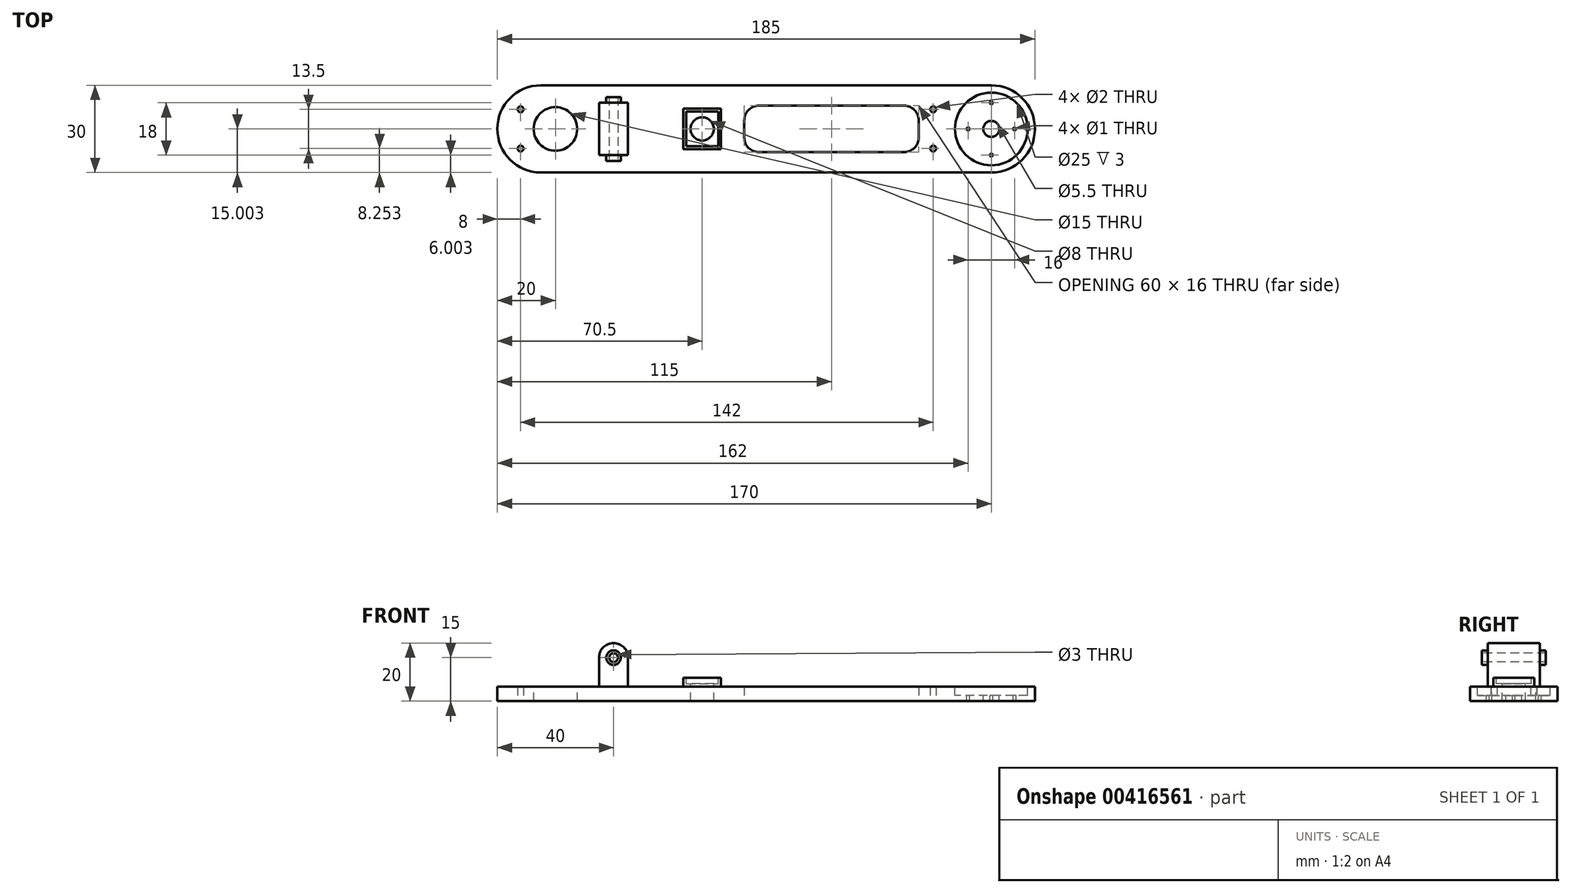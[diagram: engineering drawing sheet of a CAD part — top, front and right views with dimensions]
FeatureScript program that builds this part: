
annotation { "Feature Type Name" : "Feature", "Feature Type Description" : "" }
export const myFeature = defineFeature(function(context is Context, id is Id, definition is map)
    precondition{}
    {
        {
            var Q0;
            Q0=qCreatedBy(makeId("Top.planeOp"),FACE);
            var sketch = newSketch(context, id + "F0", { "sketchPlane" : qUnion([Q0])});
            skLineSegment(sketch, "E0.bottom", {"start": v(-85, 3.1) * mm, "end": v(100, 3.1) * mm});
            skLineSegment(sketch, "E0.top", {"start": v(-85, -26.9) * mm, "end": v(100, -26.9) * mm});
            skLineSegment(sketch, "E0.left", {"start": v(-85, 3.1) * mm, "end": v(-85, -26.9) * mm});
            skLineSegment(sketch, "E0.right", {"start": v(100, 3.1) * mm, "end": v(100, -26.9) * mm});
            skCircle(sketch, "E1", {"center": v(65, -5.15) * mm, "radius": 1 * mm});
            skCircle(sketch, "E2", {"center": v(65, -18.65) * mm, "radius": 1 * mm});
            skCircle(sketch, "E3", {"center": v(-77, -5.15) * mm, "radius": 1 * mm});
            skCircle(sketch, "E4", {"center": v(-77, -18.65) * mm, "radius": 1 * mm});
            skLineSegment(sketch, "E5.bottom", {"start": v(0, -3.9) * mm, "end": v(60, -3.9) * mm});
            skLineSegment(sketch, "E5.top", {"start": v(0, -19.9) * mm, "end": v(60, -19.9) * mm});
            skLineSegment(sketch, "E5.left", {"start": v(0, -3.9) * mm, "end": v(0, -19.9) * mm});
            skLineSegment(sketch, "E5.right", {"start": v(60, -3.9) * mm, "end": v(60, -19.9) * mm});
            skSolve(sketch);
        }
        {
            var Q0;
            Q0=makeQuery(id+"F0.imprint","IMPRINT",FACE,{"disambiguationData":[TD([[makeQuery(id+"F0.imprint","IMPRINT",EDGE,{"derivedFrom":sQuery(id+"F0.wireOp",EDGE,"E0.bottom")}),-1.0]])]});
            extrude(context, id + "F1", {"entities" : qUnion([Q0]), "depth" : 5 * mm});
        }
        {
            var Q0;
            Q0=makeQuery(id+"F1.opExtrude","CAP_FACE",FACE,{"disambiguationData":[OSD([sQuery(id+"F0.wireOp",EDGE,"E0.bottom"),sQuery(id+"F0.wireOp",EDGE,"E0.top"),sQuery(id+"F0.wireOp",EDGE,"E0.left"),sQuery(id+"F0.wireOp",EDGE,"E0.right")])],"isStart":false});
            var sketch = newSketch(context, id + "F2", { "sketchPlane" : qUnion([Q0])});
            skCircle(sketch, "E6", {"center": v(85, -11.9) * mm, "radius": 12.5 * mm});
            skCircle(sketch, "E7", {"center": v(85, -11.9) * mm, "radius": 2.75 * mm});
            skCircle(sketch, "E8", {"center": v(85, -2.9) * mm, "radius": 0.5 * mm});
            skCircle(sketch, "E9", {"center": v(85, -20.9) * mm, "radius": 0.5 * mm});
            skCircle(sketch, "E10", {"center": v(93, -11.9) * mm, "radius": 0.5 * mm});
            skCircle(sketch, "E11", {"center": v(77, -11.9) * mm, "radius": 0.5 * mm});
            skCircle(sketch, "E12", {"center": v(-65, -11.9) * mm, "radius": 7.5 * mm});
            skLineSegment(sketch, "E13.bottom", {"start": v(-50, -2.9) * mm, "end": v(-40, -2.9) * mm});
            skLineSegment(sketch, "E13.top", {"start": v(-50, -20.9) * mm, "end": v(-40, -20.9) * mm});
            skLineSegment(sketch, "E13.left", {"start": v(-50, -2.9) * mm, "end": v(-50, -20.9) * mm});
            skLineSegment(sketch, "E13.right", {"start": v(-40, -2.9) * mm, "end": v(-40, -20.9) * mm});
            skLineSegment(sketch, "E14.bottom", {"start": v(-21, -4.9) * mm, "end": v(-8, -4.9) * mm});
            skLineSegment(sketch, "E14.top", {"start": v(-21, -18.9) * mm, "end": v(-8, -18.9) * mm});
            skLineSegment(sketch, "E14.left", {"start": v(-21, -4.9) * mm, "end": v(-21, -18.9) * mm});
            skLineSegment(sketch, "E14.right", {"start": v(-8, -4.9) * mm, "end": v(-8, -18.9) * mm});
            skSolve(sketch);
        }
        {
            var Q0;
            Q0=makeQuery(id+"F2.imprint","IMPRINT",FACE,{"disambiguationData":[TD([[makeQuery(id+"F2.imprint","IMPRINT",EDGE,{"derivedFrom":sQuery(id+"F2.wireOp",EDGE,"E6")}),1.0]])]});
            extrude(context, id + "F3", {"entities" : qUnion([Q0]), "operationType" : NewBodyOperationType.REMOVE, "oppositeDirection" : true, "depth" : 3 * mm});
        }
        {
            var Q0;
            Q0=makeQuery(id+"F2.imprint","IMPRINT",FACE,{"disambiguationData":[TD([[makeQuery(id+"F2.imprint","IMPRINT",EDGE,{"derivedFrom":sQuery(id+"F2.wireOp",EDGE,"E7")}),1.0]])]});
            var Q1;
            Q1=makeQuery(id+"F2.imprint","IMPRINT",FACE,{"disambiguationData":[TD([[makeQuery(id+"F2.imprint","IMPRINT",EDGE,{"derivedFrom":sQuery(id+"F2.wireOp",EDGE,"E8")}),1.0]])]});
            var Q2;
            Q2=makeQuery(id+"F2.imprint","IMPRINT",FACE,{"disambiguationData":[TD([[makeQuery(id+"F2.imprint","IMPRINT",EDGE,{"derivedFrom":sQuery(id+"F2.wireOp",EDGE,"E11")}),1.0]])]});
            var Q3;
            Q3=makeQuery(id+"F2.imprint","IMPRINT",FACE,{"disambiguationData":[TD([[makeQuery(id+"F2.imprint","IMPRINT",EDGE,{"derivedFrom":sQuery(id+"F2.wireOp",EDGE,"E9")}),1.0]])]});
            var Q4;
            Q4=makeQuery(id+"F2.imprint","IMPRINT",FACE,{"disambiguationData":[TD([[makeQuery(id+"F2.imprint","IMPRINT",EDGE,{"derivedFrom":sQuery(id+"F2.wireOp",EDGE,"E10")}),1.0]])]});
            extrude(context, id + "F4", {"entities" : qUnion([Q0, Q1, Q2, Q3, Q4]), "operationType" : NewBodyOperationType.REMOVE, "oppositeDirection" : true, "depth" : 25 * mm});
        }
        {
            var Q0;
            Q0=makeQuery(id+"F1.opExtrude","SWEPT_EDGE",EDGE,{"disambiguationData":[OSD([sQuery(id+"F0.wireOp",EDGE,"E0.bottom"),sQuery(id+"F0.wireOp",EDGE,"E0.right")])]});
            var Q1;
            Q1=makeQuery(id+"F1.opExtrude","SWEPT_EDGE",EDGE,{"disambiguationData":[OSD([sQuery(id+"F0.wireOp",EDGE,"E0.top"),sQuery(id+"F0.wireOp",EDGE,"E0.right")])]});
            var Q2;
            Q2=makeQuery(id+"F1.opExtrude","SWEPT_EDGE",EDGE,{"disambiguationData":[OSD([sQuery(id+"F0.wireOp",EDGE,"E0.top"),sQuery(id+"F0.wireOp",EDGE,"E0.left")])]});
            var Q3;
            Q3=makeQuery(id+"F1.opExtrude","SWEPT_EDGE",EDGE,{"disambiguationData":[OSD([sQuery(id+"F0.wireOp",EDGE,"E0.bottom"),sQuery(id+"F0.wireOp",EDGE,"E0.left")])]});
            fillet(context, id + "F5", {"entities" : qUnion([Q0, Q1, Q2, Q3]), "radius" : 15 * mm, "tangentPropagation" : true, "allowEdgeOverflow" : false});
        }
        {
            var Q0;
            Q0=makeQuery(id+"F2.imprint","IMPRINT",FACE,{"disambiguationData":[TD([[makeQuery(id+"F2.imprint","IMPRINT",EDGE,{"derivedFrom":sQuery(id+"F2.wireOp",EDGE,"E12")}),1.0]])]});
            extrude(context, id + "F6", {"entities" : qUnion([Q0]), "operationType" : NewBodyOperationType.REMOVE, "oppositeDirection" : true, "depth" : 25 * mm});
        }
        {
            var Q0;
            Q0=makeQuery(id+"F2.imprint","IMPRINT",FACE,{"disambiguationData":[TD([[makeQuery(id+"F2.imprint","IMPRINT",EDGE,{"derivedFrom":sQuery(id+"F2.wireOp",EDGE,"E13.bottom")}),-1.0]])]});
            extrude(context, id + "F7", {"entities" : qUnion([Q0]), "operationType" : NewBodyOperationType.ADD, "depth" : 15 * mm});
        }
        {
            var Q0;
            Q0=makeQuery(id+"F7.opExtrude","CAP_EDGE",EDGE,{"disambiguationData":[OSD([sQuery(id+"F2.wireOp",EDGE,"E13.left")])],"isStart":true});
            var Q1;
            Q1=makeQuery(id+"F7.opExtrude","CAP_EDGE",EDGE,{"disambiguationData":[OSD([sQuery(id+"F2.wireOp",EDGE,"E13.right")])],"isStart":false});
            var Q2;
            Q2=makeQuery(id+"F7.opExtrude","CAP_EDGE",EDGE,{"disambiguationData":[OSD([sQuery(id+"F2.wireOp",EDGE,"E13.left")])],"isStart":false});
            var Q3;
            Q3=makeQuery(id+"F7.opExtrude","CAP_EDGE",EDGE,{"disambiguationData":[OSD([sQuery(id+"F2.wireOp",EDGE,"E13.right")])],"isStart":true});
            fillet(context, id + "F8", {"entities" : qUnion([Q0, Q1, Q2, Q3]), "radius" : 5 * mm, "tangentPropagation" : true, "allowEdgeOverflow" : false});
        }
        {
            var Q0;
            Q0=makeQuery(id+"F7.opExtrude","SWEPT_FACE",FACE,{"disambiguationData":[OSD([sQuery(id+"F2.wireOp",EDGE,"E13.top")])]});
            var sketch = newSketch(context, id + "F9", { "sketchPlane" : qUnion([Q0])});
            skCircle(sketch, "E15", {"center": v(-45, 15) * mm, "radius": 1.5 * mm});
            skCircle(sketch, "E16", {"center": v(-45, 15) * mm, "radius": 2.5 * mm});
            skSolve(sketch);
        }
        {
            var Q0;
            Q0=makeQuery(id+"F9.imprint","IMPRINT",FACE,{"disambiguationData":[TD([[makeQuery(id+"F9.imprint","IMPRINT",EDGE,{"derivedFrom":sQuery(id+"F9.wireOp",EDGE,"E15")}),1.0]])]});
            extrude(context, id + "F10", {"entities" : qUnion([Q0]), "operationType" : NewBodyOperationType.REMOVE, "oppositeDirection" : true, "depth" : 25 * mm});
        }
        {
            var Q0;
            Q0=makeQuery(id+"F9.imprint","IMPRINT",FACE,{"disambiguationData":[TD([[makeQuery(id+"F9.imprint","IMPRINT",EDGE,{"derivedFrom":sQuery(id+"F9.wireOp",EDGE,"E15")}),-1.0]])]});
            extrude(context, id + "F11", {"entities" : qUnion([Q0]), "operationType" : NewBodyOperationType.ADD, "depth" : 2 * mm});
        }
        {
            var Q0;
            Q0=makeQuery(id+"F7.opExtrude","SWEPT_FACE",FACE,{"disambiguationData":[OSD([sQuery(id+"F2.wireOp",EDGE,"E13.bottom")])]});
            var sketch = newSketch(context, id + "F12", { "sketchPlane" : qUnion([Q0])});
            skCircle(sketch, "E17", {"center": v(45, 15) * mm, "radius": 2.5 * mm});
            skSolve(sketch);
        }
        {
            var Q0;
            Q0=makeQuery(id+"F12.imprint","IMPRINT",FACE,{"disambiguationData":[TD([[makeQuery(id+"F12.imprint","IMPRINT",EDGE,{"derivedFrom":sQuery(id+"F12.wireOp",EDGE,"E17")}),1.0]])]});
            extrude(context, id + "F13", {"entities" : qUnion([Q0]), "operationType" : NewBodyOperationType.ADD, "depth" : 2 * mm});
        }
        {
            var Q0;
            Q0=makeQuery(id+"F2.imprint","IMPRINT",FACE,{"disambiguationData":[TD([[makeQuery(id+"F2.imprint","IMPRINT",EDGE,{"derivedFrom":sQuery(id+"F2.wireOp",EDGE,"E14.bottom")}),-1.0]])]});
            extrude(context, id + "F14", {"entities" : qUnion([Q0]), "operationType" : NewBodyOperationType.ADD, "depth" : 3 * mm});
        }
        {
            var Q0;
            Q0=makeQuery(id+"F14.opExtrude","CAP_FACE",FACE,{"disambiguationData":[OSD([sQuery(id+"F2.wireOp",EDGE,"E14.bottom"),sQuery(id+"F2.wireOp",EDGE,"E14.top"),sQuery(id+"F2.wireOp",EDGE,"E14.left"),sQuery(id+"F2.wireOp",EDGE,"E14.right")])],"isStart":false});
            var sketch = newSketch(context, id + "F15", { "sketchPlane" : qUnion([Q0])});
            skLineSegment(sketch, "E18.bottom", {"start": v(-20, -5.9) * mm, "end": v(-9, -5.9) * mm});
            skLineSegment(sketch, "E18.top", {"start": v(-20, -17.9) * mm, "end": v(-9, -17.9) * mm});
            skLineSegment(sketch, "E18.left", {"start": v(-20, -5.9) * mm, "end": v(-20, -17.9) * mm});
            skLineSegment(sketch, "E18.right", {"start": v(-9, -5.9) * mm, "end": v(-9, -17.9) * mm});
            skCircle(sketch, "E19", {"center": v(-14.5, -11.9) * mm, "radius": 4 * mm});
            skSolve(sketch);
        }
        {
            var Q0;
            Q0=makeQuery(id+"F15.imprint","IMPRINT",FACE,{"disambiguationData":[TD([[makeQuery(id+"F15.imprint","IMPRINT",EDGE,{"derivedFrom":sQuery(id+"F15.wireOp",EDGE,"E18.bottom")}),-1.0]])]});
            extrude(context, id + "F16", {"entities" : qUnion([Q0]), "operationType" : NewBodyOperationType.REMOVE, "oppositeDirection" : true, "depth" : 2 * mm});
        }
        {
            var Q0;
            Q0=makeQuery(id+"F16.boolean.opBoolean","SPLIT",FACE,{"disambiguationData":[TD([makeQuery(id+"F16.opExtrude","SWEPT_FACE",FACE,{"disambiguationData":[OSD([sQuery(id+"F15.wireOp",EDGE,"E19")])]})])],"derivedFrom":makeQuery(id+"F14.opExtrude","CAP_FACE",FACE,{"disambiguationData":[OSD([sQuery(id+"F2.wireOp",EDGE,"E14.bottom"),sQuery(id+"F2.wireOp",EDGE,"E14.top"),sQuery(id+"F2.wireOp",EDGE,"E14.left"),sQuery(id+"F2.wireOp",EDGE,"E14.right")])],"isStart":false})});
            extrude(context, id + "F17", {"entities" : qUnion([Q0]), "operationType" : NewBodyOperationType.REMOVE, "oppositeDirection" : true, "depth" : 25 * mm});
        }
        {
            var Q0;
            Q0=makeQuery(id+"F1.opExtrude","SWEPT_EDGE",EDGE,{"disambiguationData":[OSD([sQuery(id+"F0.wireOp",EDGE,"E5.bottom"),sQuery(id+"F0.wireOp",EDGE,"E5.left")])]});
            var Q1;
            Q1=makeQuery(id+"F1.opExtrude","SWEPT_EDGE",EDGE,{"disambiguationData":[OSD([sQuery(id+"F0.wireOp",EDGE,"E5.top"),sQuery(id+"F0.wireOp",EDGE,"E5.left")])]});
            var Q2;
            Q2=makeQuery(id+"F1.opExtrude","SWEPT_EDGE",EDGE,{"disambiguationData":[OSD([sQuery(id+"F0.wireOp",EDGE,"E5.bottom"),sQuery(id+"F0.wireOp",EDGE,"E5.right")])]});
            var Q3;
            Q3=makeQuery(id+"F1.opExtrude","SWEPT_EDGE",EDGE,{"disambiguationData":[OSD([sQuery(id+"F0.wireOp",EDGE,"E5.top"),sQuery(id+"F0.wireOp",EDGE,"E5.right")])]});
            fillet(context, id + "F18", {"entities" : qUnion([Q0, Q1, Q2, Q3]), "radius" : 5 * mm, "tangentPropagation" : true, "allowEdgeOverflow" : false});
        }
    });
